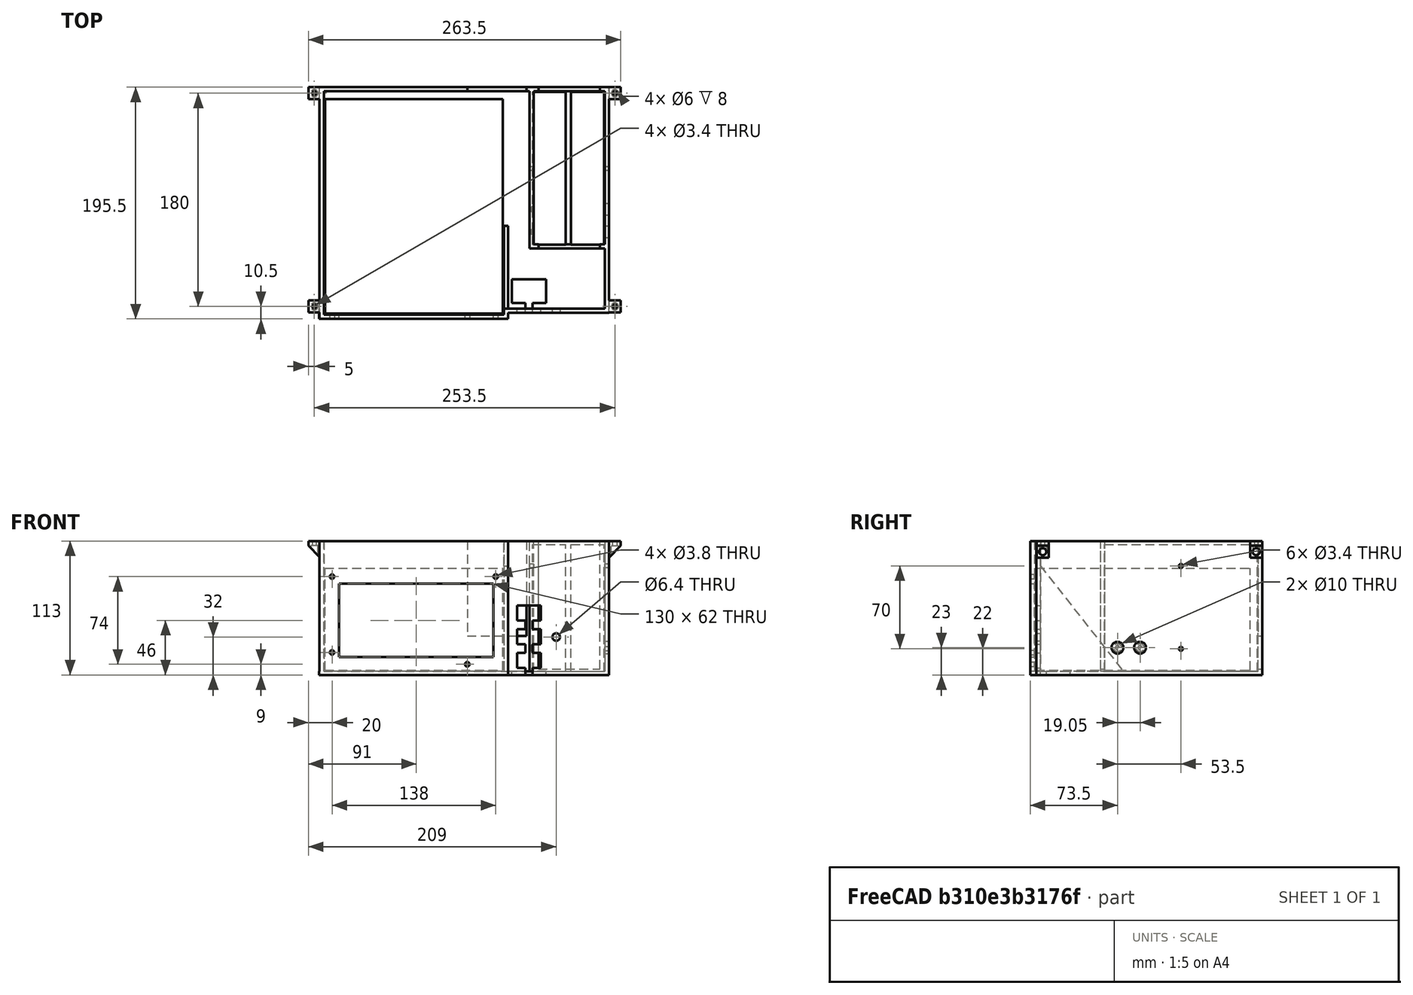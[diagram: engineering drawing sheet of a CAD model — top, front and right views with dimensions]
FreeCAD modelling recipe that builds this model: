
FCSTD DOCUMENT  (FreeCAD 0.20R2887)
Label: HiCoHolderPt3
License: All rights reserved
LicenseURL: http://en.wikipedia.org/wiki/All_rights_reserved
objects: Part::Box×32, Part::Cylinder×19, Part::MultiFuse×18, Part::Cut×11, Part::Wedge×5, Part::Cone×2
note: 87 computed .brp shape members not serialized (recipe doc carries the construction recipe); baked Part::Feature solids carry a one-line shape summary decoded from their .brp

FEATURE [Part::Box] Box  label="PSUPanelPlate"
  AttacherType = Attacher::AttachEngine3D
  Height = 113
  Length = 156
  Placement = pos=(-3,-3.5,-3) rot=(0,0,1;0rad)
  Width = 3.5
FEATURE [Part::Box] Box001  label="PSUblob"
  AttacherType = Attacher::AttachEngine3D
  Height = 86
  Length = 150
  Placement = pos=(0,-4,1) rot=(0,0,1;0rad)
  Width = 181
FEATURE [Part::Box] Box002  label="Cube001"
  AttacherType = Attacher::AttachEngine3D
  Height = 62
  Length = 130
  Placement = pos=(12,-3.5,12) rot=(0,0,1;0rad)
  Width = 3.5
FEATURE [Part::Cylinder] Cylinder
  Angle = 360
  AttacherType = Attacher::AttachEngine3D
  FirstAngle = 0
  Height = 10
  Placement = pos=(6,0,16) rot=(1,0,0;1.5708rad)
  Radius = 1.9
  SecondAngle = 0
FEATURE [Part::Cylinder] Cylinder001
  Angle = 360
  AttacherType = Attacher::AttachEngine3D
  FirstAngle = 0
  Height = 10
  Placement = pos=(6,0,80) rot=(1,0,0;1.5708rad)
  Radius = 1.9
  SecondAngle = 0
FEATURE [Part::Cylinder] Cylinder002
  Angle = 360
  AttacherType = Attacher::AttachEngine3D
  FirstAngle = 0
  Height = 10
  Placement = pos=(144,0,80) rot=(1,0,0;1.5708rad)
  Radius = 1.9
  SecondAngle = 0
FEATURE [Part::Cylinder] Cylinder003
  Angle = 360
  AttacherType = Attacher::AttachEngine3D
  FirstAngle = 0
  Height = 10
  Placement = pos=(120,0,6) rot=(1,0,0;1.5708rad)
  Radius = 1.9
  SecondAngle = 0
FEATURE [Part::MultiFuse] Fusion  label="PSU PanelHoles"
  Shapes = -> [Cylinder,Cylinder001,Cylinder002,Cylinder003,Box002]
FEATURE [Part::Cut] Cut  label="PSUPanel"
  Base = -> Box
  Placement = pos=(0,-5,0) rot=(0,0,1;0rad)
  Tool = -> Fusion
FEATURE [Part::Box] Box003  label="BasePlate"
  AttacherType = Attacher::AttachEngine3D
  Height = 3
  Length = 244
  Placement = pos=(-4.5,0,-3) rot=(0,0,1;0rad)
  Width = 186
FEATURE [Part::Cylinder] Cylinder004  label="PowerConnectorScrew2"
  Angle = 360
  AttacherType = Attacher::AttachEngine3D
  FirstAngle = 0
  Height = 10
  Radius = 1.7
  SecondAngle = 0
FEATURE [Part::Cylinder] Cylinder005  label="PowerConnectorScrew1"
  Angle = 360
  AttacherType = Attacher::AttachEngine3D
  FirstAngle = 0
  Height = 10
  Placement = pos=(0,19.05,0) rot=(0,0,1;0rad)
  Radius = 1.7
  SecondAngle = 0
FEATURE [Part::Wedge] Wedge001  label="RightPSUPanelSupport"
  AttacherType = Attacher::AttachEngine3D
  Placement = pos=(151,0,0) rot=(0,0,1;0rad)
  X2max = 3.5
  X2min = 0
  Xmax = 3.5
  Xmin = 0
  Ymax = 70
  Ymin = 0
  Z2max = 0
  Z2min = -3
  Zmax = 89
  Zmin = -3
FEATURE [Part::Box] Box004  label="SwitchPanel"
  AttacherType = Attacher::AttachEngine3D
  Height = 113
  Length = 86.5
  Placement = pos=(153,-3.5,-3) rot=(0,0,1;0rad)
  Width = 3.5
FEATURE [Part::Box] Box006  label="Cube003"
  AttacherType = Attacher::AttachEngine3D
  Height = 19.2
  Length = 6
  Placement = pos=(164,-3.5,-6) rot=(0,0,1;0rad)
  Width = 3.5
FEATURE [Part::Box] Box007  label="Cube004"
  AttacherType = Attacher::AttachEngine3D
  Height = 12.7
  Length = 20
  Placement = pos=(157,-3.5,3) rot=(0,0,1;0rad)
  Width = 3.5
FEATURE [Part::Box] Box008  label="Cube005"
  AttacherType = Attacher::AttachEngine3D
  Height = 19.2
  Length = 6
  Placement = pos=(164,-3.5,-6) rot=(0,0,1;0rad)
  Width = 3.5
FEATURE [Part::MultiFuse] Fusion003  label="ButtonCutout001"
  Placement = pos=(5,0,20) rot=(0,0,1;0rad)
  Shapes = -> [Box007,Box008]
FEATURE [Part::Box] Box009  label="Cube006"
  AttacherType = Attacher::AttachEngine3D
  Height = 12.7
  Length = 20
  Placement = pos=(157,-3.5,3) rot=(0,0,1;0rad)
  Width = 3.5
FEATURE [Part::Box] Box010  label="Cube007"
  AttacherType = Attacher::AttachEngine3D
  Height = 19.2
  Length = 6
  Placement = pos=(164,-3.5,-6) rot=(0,0,1;0rad)
  Width = 3.5
FEATURE [Part::MultiFuse] Fusion004  label="ButtonCutout002"
  Placement = pos=(5,0,40) rot=(0,0,1;0rad)
  Shapes = -> [Box009,Box010]
FEATURE [Part::Cylinder] Cylinder006
  Angle = 360
  AttacherType = Attacher::AttachEngine3D
  FirstAngle = 0
  Height = 10
  Placement = pos=(195,0,29) rot=(1,0,0;1.5708rad)
  Radius = 3.2
  SecondAngle = 0
FEATURE [Part::Box] Box011  label="NetLionblob"
  AttacherType = Attacher::AttachEngine3D
  Height = 107
  Length = 28
  Placement = pos=(207.5,54,0) rot=(0,0,1;0rad)
  Width = 129
FEATURE [Part::Box] Box012  label="NetLionblob001"
  AttacherType = Attacher::AttachEngine3D
  Height = 107
  Length = 28
  Placement = pos=(175,54,0) rot=(0,0,1;0rad)
  Width = 129
FEATURE [Part::Box] Box013  label="OuterBox"
  AttacherType = Attacher::AttachEngine3D
  Height = 113
  Length = 67
  Placement = pos=(179.5,51,-3) rot=(0,0,1;0rad)
  Width = 136
FEATURE [Part::Box] Box014  label="Cube008"
  AttacherType = Attacher::AttachEngine3D
  Height = 113
  Length = 60
  Placement = pos=(183,54.5,0) rot=(0,0,1;0rad)
  Width = 129
FEATURE [Part::Box] Box015  label="Cube009"
  AttacherType = Attacher::AttachEngine3D
  Height = 113
  Length = 52
  Placement = pos=(187,51,2) rot=(0,0,1;0rad)
  Width = 136
FEATURE [Part::MultiFuse] Fusion006  label="NetLionCutouts"
  Shapes = -> [Box015,Box014]
FEATURE [Part::Cut] Cut003  label="SlicedBox"
  Base = -> Box013
  Tool = -> Fusion006
FEATURE [Part::Cone] Cone  label="PowerConnectorScrewCountersink1"
  Angle = 360
  AttacherType = Attacher::AttachEngine3D
  Height = 3.8278
  Radius1 = 3.3264
  Radius2 = 0
FEATURE [Part::Cone] Cone001  label="PowerConnectorScrewCountersink2"
  Angle = 360
  AttacherType = Attacher::AttachEngine3D
  Height = 3.83
  Placement = pos=(0,19.05,0) rot=(0,0,1;0rad)
  Radius1 = 3.33
  Radius2 = 0
FEATURE [Part::Cylinder] Cylinder007  label="ScrewdriverAccess2"
  Angle = 360
  AttacherType = Attacher::AttachEngine3D
  FirstAngle = 0
  Height = 10
  Placement = pos=(0,0,-66) rot=(0,0,1;0rad)
  Radius = 5
  SecondAngle = 0
FEATURE [Part::Cylinder] Cylinder008  label="ScrewdriverAccess1"
  Angle = 360
  AttacherType = Attacher::AttachEngine3D
  FirstAngle = 0
  Height = 10
  Placement = pos=(0,19.05,-66) rot=(0,0,1;0rad)
  Radius = 5
  SecondAngle = 0
FEATURE [Part::MultiFuse] Fusion001  label="PowerConnectorHoles"
  Placement = pos=(183,65,20) rot=(0,1,0;-1.5708rad)
  Shapes = -> [Cylinder005,Cylinder004,Cone,Cone001,Cylinder008,Cylinder007]
FEATURE [Part::Cut] Cut004  label="BoxWithPowerConnector"
  Base = -> Cut003
  Tool = -> Fusion001
FEATURE [Part::Cylinder] Cylinder009
  Angle = 360
  AttacherType = Attacher::AttachEngine3D
  FirstAngle = 0
  Height = 100
  Placement = pos=(0,0,0) rot=(0,1,0;1.5708rad)
  Radius = 1.7
  SecondAngle = 0
FEATURE [Part::Cylinder] Cylinder010
  Angle = 360
  AttacherType = Attacher::AttachEngine3D
  FirstAngle = 0
  Height = 100
  Placement = pos=(0,70,0) rot=(0,1,0;1.5708rad)
  Radius = 1.7
  SecondAngle = 0
FEATURE [Part::MultiFuse] Fusion007  label="NetLionMountHoles"
  Placement = pos=(179,118.5,19) rot=(1,0,0;1.5708rad)
  Shapes = -> [Cylinder010,Cylinder009]
FEATURE [Part::Cut] Cut005  label="NetLionMountBox"
  Base = -> Cut004
  Placement = pos=(-7,0,0) rot=(0,0,1;0rad)
  Tool = -> Fusion007
FEATURE [Part::Box] Box016  label="Cube"
  AttacherType = Attacher::AttachEngine3D
  Height = 110
  Length = 3
  Placement = pos=(-4,-3,0) rot=(0,0,1;0rad)
  Width = 10
FEATURE [Part::Box] Box017  label="Cube010"
  AttacherType = Attacher::AttachEngine3D
  Height = 4
  Length = 13
  Placement = pos=(-14,-3,106) rot=(0,0,1;0rad)
  Width = 10
FEATURE [Part::Cylinder] Cylinder011
  Angle = 360
  AttacherType = Attacher::AttachEngine3D
  FirstAngle = 0
  Height = 40
  Placement = pos=(-9,2,70) rot=(0,0,1;0rad)
  Radius = 1.7
  SecondAngle = 0
FEATURE [Part::Cylinder] Cylinder012
  Angle = 360
  AttacherType = Attacher::AttachEngine3D
  FirstAngle = 0
  Height = 36
  Placement = pos=(-9,2,70) rot=(0,0,1;0rad)
  Radius = 3
  SecondAngle = 0
FEATURE [Part::Wedge] Wedge002  label="Wedge"
  AttacherType = Attacher::AttachEngine3D
  Placement = pos=(-4,-3,96) rot=(0,0,1;1.5708rad)
  X2max = 10
  X2min = 0
  Xmax = 10
  Xmin = 0
  Ymax = 10
  Ymin = 0
  Z2max = 10
  Z2min = 10
  Zmax = 10
  Zmin = 0
FEATURE [Part::MultiFuse] Fusion008  label="SupportArm"
  Shapes = -> [Box016,Box017,Wedge002]
FEATURE [Part::MultiFuse] Fusion009  label="CounterboredHole"
  Shapes = -> [Cylinder012,Cylinder011]
FEATURE [Part::Cut] Cut006  label="Mount"
  Base = -> Fusion008
  Tool = -> Fusion009
FEATURE [Part::Box] Box018  label="Cube011"
  AttacherType = Attacher::AttachEngine3D
  Height = 4
  Length = 13
  Placement = pos=(-14,-3,106) rot=(0,0,1;0rad)
  Width = 10
FEATURE [Part::Cylinder] Cylinder013
  Angle = 360
  AttacherType = Attacher::AttachEngine3D
  FirstAngle = 0
  Height = 40
  Placement = pos=(-9,2,70) rot=(0,0,1;0rad)
  Radius = 1.7
  SecondAngle = 0
FEATURE [Part::Cylinder] Cylinder014
  Angle = 360
  AttacherType = Attacher::AttachEngine3D
  FirstAngle = 0
  Height = 36
  Placement = pos=(-9,2,70) rot=(0,0,1;0rad)
  Radius = 3
  SecondAngle = 0
FEATURE [Part::MultiFuse] Fusion011  label="CounterboredHole001"
  Shapes = -> [Cylinder014,Cylinder013]
FEATURE [Part::Wedge] Wedge003
  AttacherType = Attacher::AttachEngine3D
  Placement = pos=(-4,-3,96) rot=(0,0,1;1.5708rad)
  X2max = 10
  X2min = 0
  Xmax = 10
  Xmin = 0
  Ymax = 10
  Ymin = 0
  Z2max = 10
  Z2min = 10
  Zmax = 10
  Zmin = 0
FEATURE [Part::Box] Box019  label="Cube012"
  AttacherType = Attacher::AttachEngine3D
  Height = 110
  Length = 3
  Placement = pos=(-4,-3,0) rot=(0,0,1;0rad)
  Width = 10
FEATURE [Part::MultiFuse] Fusion010  label="SupportArm001"
  Shapes = -> [Box019,Box018,Wedge003]
FEATURE [Part::Cut] Cut007  label="Mount001"
  Base = -> Fusion010
  Placement = pos=(0,180,0) rot=(0,0,1;0rad)
  Tool = -> Fusion011
FEATURE [Part::Box] Box020  label="Cube013"
  AttacherType = Attacher::AttachEngine3D
  Height = 4
  Length = 13.5
  Placement = pos=(-14,-3,106) rot=(0,0,1;0rad)
  Width = 10
FEATURE [Part::Cylinder] Cylinder015
  Angle = 360
  AttacherType = Attacher::AttachEngine3D
  FirstAngle = 0
  Height = 40
  Placement = pos=(-9,2,70) rot=(0,0,1;0rad)
  Radius = 1.7
  SecondAngle = 0
FEATURE [Part::Cylinder] Cylinder016
  Angle = 360
  AttacherType = Attacher::AttachEngine3D
  FirstAngle = 0
  Height = 36
  Placement = pos=(-9,2,70) rot=(0,0,1;0rad)
  Radius = 3
  SecondAngle = 0
FEATURE [Part::MultiFuse] Fusion013  label="CounterboredHole002"
  Shapes = -> [Cylinder016,Cylinder015]
FEATURE [Part::Wedge] Wedge004
  AttacherType = Attacher::AttachEngine3D
  Placement = pos=(-4,-3,96) rot=(0,0,1;1.5708rad)
  X2max = 10
  X2min = 0
  Xmax = 10
  Xmin = 0
  Ymax = 10
  Ymin = 0
  Z2max = 10
  Z2min = 10
  Zmax = 10
  Zmin = 0
FEATURE [Part::Box] Box021  label="Cube014"
  AttacherType = Attacher::AttachEngine3D
  Height = 110
  Length = 3.5
  Placement = pos=(-4,-3,0) rot=(0,0,1;0rad)
  Width = 10
FEATURE [Part::MultiFuse] Fusion012  label="SupportArm002"
  Shapes = -> [Box021,Box020,Wedge004]
FEATURE [Part::Cut] Cut008  label="Mount002"
  Base = -> Fusion012
  Placement = pos=(235.5,4,0) rot=(0,0,1;3.14159rad)
  Tool = -> Fusion013
FEATURE [Part::Cylinder] Cylinder017
  Angle = 360
  AttacherType = Attacher::AttachEngine3D
  FirstAngle = 0
  Height = 36
  Placement = pos=(-9,2,70) rot=(0,0,1;0rad)
  Radius = 3
  SecondAngle = 0
FEATURE [Part::Box] Box022  label="Cube015"
  AttacherType = Attacher::AttachEngine3D
  Height = 110
  Length = 3.5
  Placement = pos=(-4,-3,0) rot=(0,0,1;0rad)
  Width = 10
FEATURE [Part::Wedge] Wedge005
  AttacherType = Attacher::AttachEngine3D
  Placement = pos=(-4,-3,96) rot=(0,0,1;1.5708rad)
  X2max = 10
  X2min = 0
  Xmax = 10
  Xmin = 0
  Ymax = 10
  Ymin = 0
  Z2max = 10
  Z2min = 10
  Zmax = 10
  Zmin = 0
FEATURE [Part::Cylinder] Cylinder018
  Angle = 360
  AttacherType = Attacher::AttachEngine3D
  FirstAngle = 0
  Height = 40
  Placement = pos=(-9,2,70) rot=(0,0,1;0rad)
  Radius = 1.7
  SecondAngle = 0
FEATURE [Part::MultiFuse] Fusion015  label="CounterboredHole003"
  Shapes = -> [Cylinder017,Cylinder018]
FEATURE [Part::Box] Box023  label="Cube016"
  AttacherType = Attacher::AttachEngine3D
  Height = 4
  Length = 13.5
  Placement = pos=(-14,-3,106) rot=(0,0,1;0rad)
  Width = 10
FEATURE [Part::MultiFuse] Fusion014  label="SupportArm003"
  Shapes = -> [Box022,Box023,Wedge005]
FEATURE [Part::Cut] Cut009  label="Mount003"
  Base = -> Fusion014
  Placement = pos=(235.5,184,0) rot=(0,0,1;3.14159rad)
  Tool = -> Fusion015
FEATURE [Part::Box] Box024  label="Cube017"
  AttacherType = Attacher::AttachEngine3D
  Height = 19.2
  Length = 6
  Placement = pos=(169,-3,-3) rot=(0,0,1;0rad)
  Width = 20
FEATURE [Part::Box] Box027  label="Cube020"
  AttacherType = Attacher::AttachEngine3D
  Height = 19.2
  Length = 29
  Placement = pos=(157.5,5,-3) rot=(0,0,1;0rad)
  Width = 20
FEATURE [Part::MultiFuse] Fusion016  label="SwitchAccessCuts"
  Shapes = -> [Box024,Box027]
FEATURE [Part::Cut] Cut010  label="Bottom"
  Base = -> Box003
  Tool = -> Fusion016
FEATURE [Part::Box] Box028  label="LeftSide"
  AttacherType = Attacher::AttachEngine3D
  Height = 113
  Length = 3.5
  Placement = pos=(-4.5,-8.5,-3) rot=(0,0,1;0rad)
  Width = 195.5
FEATURE [Part::Box] Box029  label="RightSide"
  AttacherType = Attacher::AttachEngine3D
  Height = 113
  Length = 3.5
  Placement = pos=(236,-3,-3) rot=(0,0,1;0rad)
  Width = 60
FEATURE [Part::Box] Box030  label="Back"
  AttacherType = Attacher::AttachEngine3D
  Height = 113
  Length = 180.5
  Placement = pos=(-3,183.5,-3) rot=(0,0,1;0rad)
  Width = 3.5
FEATURE [Part::Box] Box031  label="CordCutout"
  AttacherType = Attacher::AttachEngine3D
  Height = 80
  Length = 50
  Placement = pos=(120,180,30) rot=(0,0,1;0rad)
  Width = 10
FEATURE [Part::Box] Box032  label="PSURightFill"
  AttacherType = Attacher::AttachEngine3D
  Height = 113
  Length = 3.5
  Placement = pos=(151,-8.5,-3) rot=(0,0,1;0rad)
  Width = 8.5
FEATURE [Part::Box] Box033  label="PSUBottomFill"
  AttacherType = Attacher::AttachEngine3D
  Height = 3
  Length = 158
  Placement = pos=(-5,-8.5,-3) rot=(0,0,1;0rad)
  Width = 8.5
FEATURE [Part::Box] Box005  label="Cube002"
  AttacherType = Attacher::AttachEngine3D
  Height = 12.7
  Length = 20
  Placement = pos=(157,-3.5,3) rot=(0,0,1;0rad)
  Width = 3.5
FEATURE [Part::MultiFuse] Fusion002  label="ButtonCutout"
  Placement = pos=(5,0,0) rot=(0,0,1;0rad)
  Shapes = -> [Box005,Box006]
FEATURE [Part::MultiFuse] Fusion005  label="SwitchHoles"
  Shapes = -> [Cylinder006,Fusion002,Fusion003,Fusion004]
FEATURE [Part::Cut] Cut002  label="SwitchMounts"
  Base = -> Box004
  Tool = -> Fusion005
FEATURE [Part::MultiFuse] Fusion017  label="HiCoAuxBox"
  Shapes = -> [Cut,Wedge001,Cut002,Cut005,Cut006,Cut007,Cut008,Cut009,Cut010,Box028,Box029,Box030,Box032,Box033]
FEATURE [Part::Cut] Cut011  label="HiCoAux"
  Base = -> Fusion017
  Tool = -> Box031
